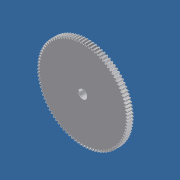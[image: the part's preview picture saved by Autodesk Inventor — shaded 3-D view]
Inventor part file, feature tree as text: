
AUTODESK INVENTOR PART (.ipt)
format: ipt  version: unknown  size: 936,960 bytes
history: native  units: in
note: dims shown in document units (in); Inventor stores cm internally (conversion verified against a paired STEP export)
features: imported_body x1, extrude x1, sketch x1
ambient origin geometry x8: Origin, YZ Plane, XZ Plane, XY Plane, X Axis, Y Axis, Z Axis, Center Point
bodies: Solid1 (feature_tree)
feature tree (3):
  imported_body  "Base1"
  extrude  "Extrusion1"  Depth=0.66in TaperAngle=0.0deg
  sketch  "Sketch1"  dims[d0=0.388in d4=0.66in d5=0.0in]
